FCSTD DOCUMENT  (FreeCAD 0.18R15671 (Git))
Label: IL_2_Verify
License: All rights reserved
LicenseURL: http://en.wikipedia.org/wiki/All_rights_reserved
objects: Part::Part2DObjectPython×100, App::DocumentObjectGroup×5, Sketcher::SketchObjectPython×1
note: 101 computed .brp shape members not serialized (recipe doc carries the construction recipe); baked Part::Feature solids carry a one-line shape summary decoded from their .brp

FEATURE [Part::Part2DObjectPython] Line  # Draft 2D object (typed FeaturePython)
  ChamferSize = 0
  Closed = false
  End = (406185,16682.9,0)
  FilletRadius = 0
  Length = 406527
  MakeFace = false
  Points = (2) [(0,0,0),(406185,16682.9,0)]
  Start = (0,0,0)
  Subdivisions = 0
FEATURE [Part::Part2DObjectPython] Line001  # Draft 2D object (typed FeaturePython)
  ChamferSize = 0
  Closed = false
  End = (393568,323876,0)
  FilletRadius = 0
  Length = 307452
  MakeFace = true
  Placement = pos=(406185,16682.9,0) rot=(0,0,1;0rad)
  Points = (2) [(0,0,0),(-12616.9,307193,0)]
  Start = (406185,16682.9,0)
  Subdivisions = 0
FEATURE [Part::Part2DObjectPython] Arc  # Draft 2D object (typed FeaturePython)
  FirstAngle = -87.6481
  LastAngle = -38.8387
  MakeFace = true
  Placement = pos=(393568,323876,0) rot=(0,0,1;0rad)
  Radius = 307452
FEATURE [Part::Part2DObjectPython] Line002  # Draft 2D object (typed FeaturePython)
  ChamferSize = 0
  Closed = false
  End = (158220,513361,0)
  FilletRadius = 0
  Length = 609600
  MakeFace = true
  Placement = pos=(633047,131064,0) rot=(0,0,1;0rad)
  Points = (2) [(0,0,0),(-474827,382298,0)]
  Start = (633047,131064,0)
  Subdivisions = 0
FEATURE [Part::Part2DObjectPython] Arc001  # Draft 2D object (typed FeaturePython)
  FirstAngle = -38.8386
  LastAngle = -29.9144
  MakeFace = true
  Placement = pos=(158220,513361,0) rot=(0,0,1;0rad)
  Radius = 609600
FEATURE [Part::Part2DObjectPython] Line003  # Draft 2D object (typed FeaturePython)
  ChamferSize = 0
  Closed = false
  End = (823746,447710,0)
  FilletRadius = 0
  Length = 274997
  MakeFace = true
  Placement = pos=(686603,209350,0) rot=(0,0,1;0rad)
  Points = (2) [(0,0,0),(137143,238359,0)]
  Start = (686603,209350,0)
  Subdivisions = 0
FEATURE [Part::Part2DObjectPython] Line009  # Draft 2D object (typed FeaturePython)
  ChamferSize = 0
  Closed = false
  End = (-180183,1.02533e+06,0)
  FilletRadius = 0
  Length = 1158240
  MakeFace = true
  Placement = pos=(823746,447710,0) rot=(0,0,1;0rad)
  Points = (2) [(0,0,0),(-1003930,577622,0)]
  Start = (823746,447710,0)
  Subdivisions = 0
FEATURE [Part::Part2DObjectPython] Arc005  # Draft 2D object (typed FeaturePython)
  FirstAngle = -29.9144
  LastAngle = 10.7592
  MakeFace = true
  Placement = pos=(-180183,1.02533e+06,0) rot=(0,0,1;0rad)
  Radius = 1158240
FEATURE [Part::Part2DObjectPython] Line010  # Draft 2D object (typed FeaturePython)
  ChamferSize = 0
  Closed = false
  End = (943133,1.31819e+06,0)
  FilletRadius = 0
  Length = 78008.6
  MakeFace = true
  Placement = pos=(957696,1.24155e+06,0) rot=(0,0,1;0rad)
  Points = (2) [(0,0,0),(-14562.8,76637.2,0)]
  Start = (957696,1.24155e+06,0)
  Subdivisions = 0
FEATURE [Part::Part2DObjectPython] Line011  # Draft 2D object (typed FeaturePython)
  ChamferSize = 0
  Closed = false
  End = (1.63185e+06,1.44906e+06,0)
  FilletRadius = 0
  Length = 701040
  MakeFace = true
  Placement = pos=(943133,1.31819e+06,0) rot=(0,0,1;0rad)
  Points = (2) [(0,0,0),(688716,130871,0)]
  Start = (943133,1.31819e+06,0)
  Subdivisions = 0
FEATURE [Part::Part2DObjectPython] Arc006  # Draft 2D object (typed FeaturePython)
  FirstAngle = -179.348
  LastAngle = -169.241
  MakeFace = true
  Placement = pos=(1.63185e+06,1.44906e+06,0) rot=(0,0,1;0rad)
  Radius = 701040
FEATURE [Part::Part2DObjectPython] Line012  # Draft 2D object (typed FeaturePython)
  ChamferSize = 0
  Closed = false
  End = (930155,1.50255e+06,0)
  FilletRadius = 0
  Length = 61471
  MakeFace = true
  Placement = pos=(930855,1.44108e+06,0) rot=(0,0,1;0rad)
  Points = (2) [(0,0,0),(-699.39,61467,0)]
  Start = (930855,1.44108e+06,0)
  Subdivisions = 0
FEATURE [Part::Part2DObjectPython] Line013  # Draft 2D object (typed FeaturePython)
  ChamferSize = 0
  Closed = false
  End = (2.14928e+06,1.51642e+06,0)
  FilletRadius = 0
  Length = 1.2192e+06
  MakeFace = true
  Placement = pos=(930155,1.50255e+06,0) rot=(0,0,1;0rad)
  Points = (2) [(0,0,0),(1219120,13871.5,0)]
  Start = (930155,1.50255e+06,0)
  Subdivisions = 0
FEATURE [Part::Part2DObjectPython] Arc007  # Draft 2D object (typed FeaturePython)
  FirstAngle = -186.169
  LastAngle = -179.348
  MakeFace = true
  Placement = pos=(2.14928e+06,1.51642e+06,0) rot=(0,0,1;0rad)
  Radius = 1.2192e+06
FEATURE [Part::Part2DObjectPython] Line014  # Draft 2D object (typed FeaturePython)
  ChamferSize = 0
  Closed = false
  End = (1.54321e+06,1.58193e+06,0)
  FilletRadius = 0
  Length = 609600
  MakeFace = true
  Placement = pos=(937137,1.64744e+06,0) rot=(0,0,1;0rad)
  Points = (2) [(0,0,0),(606070,-65510.3,0)]
  Start = (937137,1.64744e+06,0)
  Subdivisions = 0
FEATURE [Part::Part2DObjectPython] Arc008  # Draft 2D object (typed FeaturePython)
  FirstAngle = 155.568
  LastAngle = 173.831
  MakeFace = true
  Placement = pos=(1.54321e+06,1.58193e+06,0) rot=(0,0,1;0rad)
  Radius = 609600
FEATURE [Part::Part2DObjectPython] Line015  # Draft 2D object (typed FeaturePython)
  ChamferSize = 0
  Closed = false
  End = (1.02017e+06,1.90446e+06,0)
  FilletRadius = 0
  Length = 77313
  MakeFace = true
  Placement = pos=(988196,1.83407e+06,0) rot=(0,0,1;0rad)
  Points = (2) [(0,0,0),(31977.9,70389.7,0)]
  Start = (988196,1.83407e+06,0)
  Subdivisions = 0
FEATURE [Part::Part2DObjectPython] Line016  # Draft 2D object (typed FeaturePython)
  ChamferSize = 0
  Closed = false
  End = (580180,2.10435e+06,0)
  FilletRadius = 0
  Length = 483270
  MakeFace = true
  Placement = pos=(1.02017e+06,1.90446e+06,0) rot=(0,0,1;0rad)
  Points = (2) [(0,0,0),(-439994,199888,0)]
  Start = (1.02017e+06,1.90446e+06,0)
  Subdivisions = 0
FEATURE [Part::Part2DObjectPython] Arc009  # Draft 2D object (typed FeaturePython)
  FirstAngle = -24.4322
  LastAngle = 4.90889
  MakeFace = true
  Placement = pos=(580180,2.10435e+06,0) rot=(0,0,1;0rad)
  Radius = 483270
FEATURE [Part::Part2DObjectPython] Line017  # Draft 2D object (typed FeaturePython)
  ChamferSize = 0
  Closed = false
  End = (1.05283e+06,2.24875e+06,0)
  FilletRadius = 0
  Length = 103421
  MakeFace = true
  Placement = pos=(1.06168e+06,2.14571e+06,0) rot=(0,0,1;0rad)
  Points = (2) [(0,0,0),(-8849.91,103042,0)]
  Start = (1.06168e+06,2.14571e+06,0)
  Subdivisions = 0
FEATURE [Part::Part2DObjectPython] Line018  # Draft 2D object (typed FeaturePython)
  ChamferSize = 0
  Closed = false
  End = (2.14608e+06,2.34264e+06,0)
  FilletRadius = 0
  Length = 1097280
  MakeFace = true
  Placement = pos=(1.05283e+06,2.24875e+06,0) rot=(0,0,1;0rad)
  Points = (2) [(0,0,0),(1093260,93896.1,0)]
  Start = (1.05283e+06,2.24875e+06,0)
  Subdivisions = 0
FEATURE [Part::Part2DObjectPython] Arc010  # Draft 2D object (typed FeaturePython)
  FirstAngle = -192.975
  LastAngle = -175.091
  MakeFace = true
  Placement = pos=(2.14608e+06,2.34264e+06,0) rot=(0,0,1;0rad)
  Radius = 1.09728e+06
FEATURE [Part::Part2DObjectPython] Line019  # Draft 2D object (typed FeaturePython)
  ChamferSize = 0
  Closed = false
  End = (1.13352e+06,2.8351e+06,0)
  FilletRadius = 0
  Length = 252532
  MakeFace = true
  Placement = pos=(1.07682e+06,2.58901e+06,0) rot=(0,0,1;0rad)
  Points = (2) [(0,0,0),(56700,246084,0)]
  Start = (1.07682e+06,2.58901e+06,0)
  Subdivisions = 0
FEATURE [Part::Part2DObjectPython] Line020  # Draft 2D object (typed FeaturePython)
  ChamferSize = 0
  Closed = false
  End = (2.91563e+06,2.42448e+06,0)
  FilletRadius = 0
  Length = 1828800
  MakeFace = true
  Placement = pos=(1.13352e+06,2.8351e+06,0) rot=(0,0,1;0rad)
  Points = (2) [(0,0,0),(1782110,-410613,0)]
  Start = (1.13352e+06,2.8351e+06,0)
  Subdivisions = 0
FEATURE [Part::Part2DObjectPython] Arc011  # Draft 2D object (typed FeaturePython)
  FirstAngle = 153.126
  LastAngle = 167.025
  MakeFace = true
  Placement = pos=(2.91563e+06,2.42448e+06,0) rot=(0,0,1;0rad)
  Radius = 1.8288e+06
FEATURE [Part::Part2DObjectPython] Line021  # Draft 2D object (typed FeaturePython)
  ChamferSize = 0
  Closed = false
  End = (2.23592e+06,2.76894e+06,0)
  FilletRadius = 0
  Length = 1066800
  MakeFace = true
  Placement = pos=(1.28434e+06,3.25117e+06,0) rot=(0,0,1;0rad)
  Points = (2) [(0,0,0),(951585,-482232,0)]
  Start = (1.28434e+06,3.25117e+06,0)
  Subdivisions = 0
FEATURE [Part::Part2DObjectPython] Arc012  # Draft 2D object (typed FeaturePython)
  FirstAngle = 143.778
  LastAngle = 153.126
  MakeFace = true
  Placement = pos=(2.23592e+06,2.76894e+06,0) rot=(0,0,1;0rad)
  Radius = 1.0668e+06
FEATURE [Part::Part2DObjectPython] Line022  # Draft 2D object (typed FeaturePython)
  ChamferSize = 0
  Closed = false
  End = (1.91525e+06,4.13648e+06,0)
  FilletRadius = 0
  Length = 913758
  MakeFace = true
  Placement = pos=(1.3753e+06,3.39932e+06,0) rot=(0,0,1;0rad)
  Points = (2) [(0,0,0),(539954,737159,0)]
  Start = (1.3753e+06,3.39932e+06,0)
  Subdivisions = 0
FEATURE [Part::Part2DObjectPython] Line023  # Draft 2D object (typed FeaturePython)
  ChamferSize = 0
  Closed = false
  End = (2.89882e+06,3.41604e+06,0)
  FilletRadius = 0
  Length = 1.2192e+06
  MakeFace = true
  Placement = pos=(1.91525e+06,4.13648e+06,0) rot=(0,0,1;0rad)
  Points = (2) [(0,0,0),(983569,-720444,0)]
  Start = (1.91525e+06,4.13648e+06,0)
  Subdivisions = 0
FEATURE [Part::Part2DObjectPython] Arc013  # Draft 2D object (typed FeaturePython)
  FirstAngle = 138.795
  LastAngle = 143.778
  MakeFace = true
  Placement = pos=(2.89882e+06,3.41604e+06,0) rot=(0,0,1;0rad)
  Radius = 1219200
FEATURE [Part::Part2DObjectPython] Line024  # Draft 2D object (typed FeaturePython)
  ChamferSize = 0
  Closed = false
  End = (2.00002e+06,4.24029e+06,0)
  FilletRadius = 0
  Length = 28041.6
  MakeFace = true
  Placement = pos=(1.98154e+06,4.21919e+06,0) rot=(0,0,1;0rad)
  Points = (2) [(0,0,0),(18472.5,21097.3,0)]
  Start = (1.98154e+06,4.21919e+06,0)
  Subdivisions = 0
FEATURE [Part::Part2DObjectPython] Line025  # Draft 2D object (typed FeaturePython)
  ChamferSize = 0
  Closed = false
  End = (-293170,6.24817e+06,0)
  FilletRadius = 0
  Length = 3048000
  MakeFace = true
  Placement = pos=(2.00002e+06,4.24029e+06,0) rot=(0,0,1;0rad)
  Points = (2) [(0,0,0),(-2293190,2007890,0)]
  Start = (2.00002e+06,4.24029e+06,0)
  Subdivisions = 0
FEATURE [Part::Part2DObjectPython] Arc014  # Draft 2D object (typed FeaturePython)
  FirstAngle = -41.205
  LastAngle = -38.3406
  MakeFace = true
  Placement = pos=(-293170,6.24817e+06,0) rot=(0,0,1;0rad)
  Radius = 3.048e+06
FEATURE [Part::Part2DObjectPython] Line026  # Draft 2D object (typed FeaturePython)
  ChamferSize = 0
  Closed = false
  End = (2.21427e+06,4.50504e+06,0)
  FilletRadius = 0
  Length = 188244
  MakeFace = true
  Placement = pos=(2.09749e+06,4.35739e+06,0) rot=(0,0,1;0rad)
  Points = (2) [(0,0,0),(116774,147647,0)]
  Start = (2.09749e+06,4.35739e+06,0)
  Subdivisions = 0
FEATURE [Part::Part2DObjectPython] Line027  # Draft 2D object (typed FeaturePython)
  ChamferSize = 0
  Closed = false
  End = (2.6924e+06,4.12688e+06,0)
  FilletRadius = 0
  Length = 609600
  MakeFace = true
  Placement = pos=(2.21427e+06,4.50504e+06,0) rot=(0,0,1;0rad)
  Points = (2) [(0,0,0),(478132,-378156,0)]
  Start = (2.21427e+06,4.50504e+06,0)
  Subdivisions = 0
FEATURE [Part::Part2DObjectPython] Arc015  # Draft 2D object (typed FeaturePython)
  FirstAngle = 121.776
  LastAngle = 141.659
  MakeFace = true
  Placement = pos=(2.6924e+06,4.12688e+06,0) rot=(0,0,1;0rad)
  Radius = 609600
FEATURE [Part::Part2DObjectPython] Line028  # Draft 2D object (typed FeaturePython)
  ChamferSize = 0
  Closed = false
  End = (2.56738e+06,4.76653e+06,0)
  FilletRadius = 0
  Length = 230563
  MakeFace = true
  Placement = pos=(2.37138e+06,4.64511e+06,0) rot=(0,0,1;0rad)
  Points = (2) [(0,0,0),(196004,121416,0)]
  Start = (2.37138e+06,4.64511e+06,0)
  Subdivisions = 0
FEATURE [Part::Part2DObjectPython] Line029  # Draft 2D object (typed FeaturePython)
  ChamferSize = 0
  Closed = false
  End = (3.17963e+06,3.77816e+06,0)
  FilletRadius = 0
  Length = 1162630
  MakeFace = true
  Placement = pos=(2.56738e+06,4.76653e+06,0) rot=(0,0,1;0rad)
  Points = (2) [(0,0,0),(612248,-988363,0)]
  Start = (2.56738e+06,4.76653e+06,0)
  Subdivisions = 0
FEATURE [Part::Part2DObjectPython] Arc016  # Draft 2D object (typed FeaturePython)
  FirstAngle = 107.677
  LastAngle = 121.776
  MakeFace = true
  Placement = pos=(3.17963e+06,3.77816e+06,0) rot=(0,0,1;0rad)
  Radius = 1.16263e+06
FEATURE [Part::Part2DObjectPython] Line030  # Draft 2D object (typed FeaturePython)
  ChamferSize = 0
  Closed = false
  End = (3.03557e+06,4.23019e+06,0)
  FilletRadius = 0
  Length = 688199
  MakeFace = true
  Placement = pos=(2.82659e+06,4.8859e+06,0) rot=(0,0,1;0rad)
  Points = (2) [(0,0,0),(208974,-655704,0)]
  Start = (2.82659e+06,4.8859e+06,0)
  Subdivisions = 0
FEATURE [Part::Part2DObjectPython] Arc017  # Draft 2D object (typed FeaturePython)
  FirstAngle = 73.1156
  LastAngle = 107.677
  MakeFace = true
  Placement = pos=(3.03557e+06,4.23019e+06,0) rot=(0,0,1;0rad)
  Radius = 688199
FEATURE [Part::Part2DObjectPython] Line031  # Draft 2D object (typed FeaturePython)
  ChamferSize = 0
  Closed = false
  End = (3.29632e+06,4.87025e+06,0)
  FilletRadius = 0
  Length = 63614.8
  MakeFace = true
  Placement = pos=(3.23545e+06,4.88872e+06,0) rot=(0,0,1;0rad)
  Points = (2) [(0,0,0),(60872.5,-18476.4,0)]
  Start = (3.23545e+06,4.88872e+06,0)
  Subdivisions = 0
FEATURE [Part::Part2DObjectPython] Line032  # Draft 2D object (typed FeaturePython)
  ChamferSize = 0
  Closed = false
  End = (3.54552e+06,5.69127e+06,0)
  FilletRadius = 0
  Length = 858012
  MakeFace = true
  Placement = pos=(3.29632e+06,4.87025e+06,0) rot=(0,0,1;0rad)
  Points = (2) [(0,0,0),(249202,821025,0)]
  Start = (3.29632e+06,4.87025e+06,0)
  Subdivisions = 0
FEATURE [Part::Part2DObjectPython] Arc018  # Draft 2D object (typed FeaturePython)
  FirstAngle = -106.884
  LastAngle = -69.0486
  MakeFace = true
  Placement = pos=(3.54552e+06,5.69127e+06,0) rot=(0,0,1;0rad)
  Radius = 858012
FEATURE [Part::Part2DObjectPython] Line033  # Draft 2D object (typed FeaturePython)
  ChamferSize = 0
  Closed = false
  End = (4.42061e+06,5.10758e+06,0)
  FilletRadius = 0
  Length = 608515
  MakeFace = true
  Placement = pos=(3.85233e+06,4.88999e+06,0) rot=(0,0,1;0rad)
  Points = (2) [(0,0,0),(568282,217590,0)]
  Start = (3.85233e+06,4.88999e+06,0)
  Subdivisions = 0
FEATURE [Part::Part2DObjectPython] Line034  # Draft 2D object (typed FeaturePython)
  ChamferSize = 0
  Closed = false
  End = (4.25495e+06,5.54024e+06,0)
  FilletRadius = 0
  Length = 463296
  MakeFace = true
  Placement = pos=(4.42061e+06,5.10758e+06,0) rot=(0,0,1;0rad)
  Points = (2) [(0,0,0),(-165663,432665,0)]
  Start = (4.42061e+06,5.10758e+06,0)
  Subdivisions = 0
FEATURE [Part::Part2DObjectPython] Arc019  # Draft 2D object (typed FeaturePython)
  FirstAngle = -69.0486
  LastAngle = -32.2072
  MakeFace = true
  Placement = pos=(4.25495e+06,5.54024e+06,0) rot=(0,0,1;0rad)
  Radius = 463296
FEATURE [Part::Part2DObjectPython] Line035  # Draft 2D object (typed FeaturePython)
  ChamferSize = 0
  Closed = false
  End = (4.67944e+06,5.3449e+06,0)
  FilletRadius = 0
  Length = 60960
  MakeFace = true
  Placement = pos=(4.64695e+06,5.29332e+06,0) rot=(0,0,1;0rad)
  Points = (2) [(0,0,0),(32490.6,51579.8,0)]
  Start = (4.64695e+06,5.29332e+06,0)
  Subdivisions = 0
FEATURE [Part::Part2DObjectPython] Line036  # Draft 2D object (typed FeaturePython)
  ChamferSize = 0
  Closed = false
  End = (5.22103e+06,5.00374e+06,0)
  FilletRadius = 0
  Length = 640080
  MakeFace = true
  Placement = pos=(4.67944e+06,5.3449e+06,0) rot=(0,0,1;0rad)
  Points = (2) [(0,0,0),(541588,-341152,0)]
  Start = (4.67944e+06,5.3449e+06,0)
  Subdivisions = 0
FEATURE [Part::Part2DObjectPython] Arc020  # Draft 2D object (typed FeaturePython)
  FirstAngle = 136.32
  LastAngle = 147.793
  MakeFace = true
  Placement = pos=(5.22103e+06,5.00374e+06,0) rot=(0,0,1;0rad)
  Radius = 640080
FEATURE [Part::Part2DObjectPython] Line037  # Draft 2D object (typed FeaturePython)
  ChamferSize = 0
  Closed = false
  End = (5.11486e+06,5.81937e+06,0)
  FilletRadius = 0
  Length = 516539
  MakeFace = true
  Placement = pos=(4.75812e+06,5.4458e+06,0) rot=(0,0,1;0rad)
  Points = (2) [(0,0,0),(356737,373565,0)]
  Start = (4.75812e+06,5.4458e+06,0)
  Subdivisions = 0
FEATURE [Part::Part2DObjectPython] Line038  # Draft 2D object (typed FeaturePython)
  ChamferSize = 0
  Closed = false
  End = (5.66594e+06,5.29311e+06,0)
  FilletRadius = 0
  Length = 762000
  MakeFace = true
  Placement = pos=(5.11486e+06,5.81937e+06,0) rot=(0,0,1;0rad)
  Points = (2) [(0,0,0),(551085,-526260,0)]
  Start = (5.11486e+06,5.81937e+06,0)
  Subdivisions = 0
FEATURE [Part::Part2DObjectPython] Arc025  # Draft 2D object (typed FeaturePython)
  FirstAngle = 96.3367
  LastAngle = 136.32
  MakeFace = true
  Placement = pos=(5.66594e+06,5.29311e+06,0) rot=(0,0,1;0rad)
  Radius = 762000
FEATURE [Part::Part2DObjectPython] Line039  # Draft 2D object (typed FeaturePython)
  ChamferSize = 0
  Closed = false
  End = (5.65333e+06,6.05839e+06,0)
  FilletRadius = 0
  Length = 71932.8
  MakeFace = true
  Placement = pos=(5.58184e+06,6.05045e+06,0) rot=(0,0,1;0rad)
  Points = (2) [(0,0,0),(71493.3,7939.29,0)]
  Start = (5.58184e+06,6.05045e+06,0)
  Subdivisions = 0
FEATURE [Part::Part2DObjectPython] Line040  # Draft 2D object (typed FeaturePython)
  ChamferSize = 0
  Closed = false
  End = (5.5398e+06,7.08081e+06,0)
  FilletRadius = 0
  Length = 1.0287e+06
  MakeFace = true
  Placement = pos=(5.65333e+06,6.05839e+06,0) rot=(0,0,1;0rad)
  Points = (2) [(0,0,0),(-113539,1022420,0)]
  Start = (5.65333e+06,6.05839e+06,0)
  Subdivisions = 0
FEATURE [Part::Part2DObjectPython] Arc026  # Draft 2D object (typed FeaturePython)
  FirstAngle = -83.6633
  LastAngle = -64.1411
  MakeFace = true
  Placement = pos=(5.5398e+06,7.08081e+06,0) rot=(0,0,1;0rad)
  Radius = 1.0287e+06
FEATURE [Part::Part2DObjectPython] Line041  # Draft 2D object (typed FeaturePython)
  ChamferSize = 0
  Closed = false
  End = (6.36716e+06,6.33866e+06,0)
  FilletRadius = 0
  Length = 420832
  MakeFace = true
  Placement = pos=(5.98847e+06,6.15511e+06,0) rot=(0,0,1;0rad)
  Points = (2) [(0,0,0),(378694,183549,0)]
  Start = (5.98847e+06,6.15511e+06,0)
  Subdivisions = 0
FEATURE [Part::Part2DObjectPython] Line042  # Draft 2D object (typed FeaturePython)
  ChamferSize = 0
  Closed = false
  End = (6.67211e+06,5.7095e+06,0)
  FilletRadius = 0
  Length = 699162
  MakeFace = true
  Placement = pos=(6.36716e+06,6.33866e+06,0) rot=(0,0,1;0rad)
  Points = (2) [(0,0,0),(304944,-629156,0)]
  Start = (6.36716e+06,6.33866e+06,0)
  Subdivisions = 0
FEATURE [Part::Part2DObjectPython] Arc027  # Draft 2D object (typed FeaturePython)
  FirstAngle = 99.3106
  LastAngle = 115.859
  MakeFace = true
  Placement = pos=(6.67211e+06,5.7095e+06,0) rot=(0,0,1;0rad)
  Radius = 699162
FEATURE [Part::Part2DObjectPython] Line043  # Draft 2D object (typed FeaturePython)
  ChamferSize = 0
  Closed = false
  End = (7.54438e+06,6.561e+06,0)
  FilletRadius = 0
  Length = 998544
  MakeFace = true
  Placement = pos=(6.55899e+06,6.39945e+06,0) rot=(0,0,1;0rad)
  Points = (2) [(0,0,0),(985389,161551,0)]
  Start = (6.55899e+06,6.39945e+06,0)
  Subdivisions = 0
FEATURE [Part::Part2DObjectPython] Line044  # Draft 2D object (typed FeaturePython)
  ChamferSize = 0
  Closed = false
  End = (7.84026e+06,4.7563e+06,0)
  FilletRadius = 0
  Length = 1.8288e+06
  MakeFace = true
  Placement = pos=(7.54438e+06,6.561e+06,0) rot=(0,0,1;0rad)
  Points = (2) [(0,0,0),(295875,-1804710,0)]
  Start = (7.54438e+06,6.561e+06,0)
  Subdivisions = 0
FEATURE [Part::Part2DObjectPython] Arc028  # Draft 2D object (typed FeaturePython)
  FirstAngle = 91.8839
  LastAngle = 99.3106
  MakeFace = true
  Placement = pos=(7.84026e+06,4.7563e+06,0) rot=(0,0,1;0rad)
  Radius = 1828800
FEATURE [Part::Part2DObjectPython] Line045  # Draft 2D object (typed FeaturePython)
  ChamferSize = 0
  Closed = false
  End = (7.84907e+06,6.58638e+06,0)
  FilletRadius = 0
  Length = 68969.2
  MakeFace = true
  Placement = pos=(7.78014e+06,6.58411e+06,0) rot=(0,0,1;0rad)
  Points = (2) [(0,0,0),(68931.9,2267.32,0)]
  Start = (7.78014e+06,6.58411e+06,0)
  Subdivisions = 0
FEATURE [Part::Part2DObjectPython] Line046  # Draft 2D object (typed FeaturePython)
  ChamferSize = 0
  Closed = false
  End = (7.83103e+06,7.13472e+06,0)
  FilletRadius = 0
  Length = 548640
  MakeFace = true
  Placement = pos=(7.84907e+06,6.58638e+06,0) rot=(0,0,1;0rad)
  Points = (2) [(0,0,0),(-18036.2,548343,0)]
  Start = (7.84907e+06,6.58638e+06,0)
  Subdivisions = 0
FEATURE [Part::Part2DObjectPython] Arc029  # Draft 2D object (typed FeaturePython)
  FirstAngle = -88.1161
  LastAngle = -77.9325
  MakeFace = true
  Placement = pos=(7.83103e+06,7.13472e+06,0) rot=(0,0,1;0rad)
  Radius = 548640
FEATURE [Part::Part2DObjectPython] Line047  # Draft 2D object (typed FeaturePython)
  ChamferSize = 0
  Closed = false
  End = (8.03927e+06,6.6182e+06,0)
  FilletRadius = 0
  Length = 95650.2
  MakeFace = true
  Placement = pos=(7.94573e+06,6.5982e+06,0) rot=(0,0,1;0rad)
  Points = (2) [(0,0,0),(93536.5,19997,0)]
  Start = (7.94573e+06,6.5982e+06,0)
  Subdivisions = 0
FEATURE [Part::Part2DObjectPython] Line048  # Draft 2D object (typed FeaturePython)
  ChamferSize = 0
  Closed = false
  End = (7.92457e+06,7.15472e+06,0)
  FilletRadius = 0
  Length = 548640
  MakeFace = true
  Placement = pos=(8.03927e+06,6.6182e+06,0) rot=(0,0,1;0rad)
  Points = (2) [(0,0,0),(-114701,536516,0)]
  Start = (8.03927e+06,6.6182e+06,0)
  Subdivisions = 0
FEATURE [Part::Part2DObjectPython] Arc030  # Draft 2D object (typed FeaturePython)
  FirstAngle = -77.9325
  LastAngle = -62.4842
  MakeFace = true
  Placement = pos=(7.92457e+06,7.15472e+06,0) rot=(0,0,1;0rad)
  Radius = 548640
FEATURE [Part::Part2DObjectPython] Line049  # Draft 2D object (typed FeaturePython)
  ChamferSize = 0
  Closed = false
  End = (1.09943e+07,1.26169e+06,0)
  FilletRadius = 0
  Length = 6.096e+06
  MakeFace = true
  Placement = pos=(8.17804e+06,6.66814e+06,0) rot=(0,0,1;0rad)
  Points = (2) [(0,0,0),(2816310,-5406440,0)]
  Start = (8.17804e+06,6.66814e+06,0)
  Subdivisions = 0
FEATURE [Part::Part2DObjectPython] Arc031  # Draft 2D object (typed FeaturePython)
  FirstAngle = 116.064
  LastAngle = 117.516
  MakeFace = true
  Placement = pos=(1.09943e+07,1.26169e+06,0) rot=(0,0,1;0rad)
  Radius = 6.096e+06
FEATURE [Part::Part2DObjectPython] Line050  # Draft 2D object (typed FeaturePython)
  ChamferSize = 0
  Closed = false
  End = (8.53989e+06,6.8473e+06,0)
  FilletRadius = 0
  Length = 249320
  MakeFace = true
  Placement = pos=(8.31593e+06,6.73776e+06,0) rot=(0,0,1;0rad)
  Points = (2) [(0,0,0),(223965,109545,0)]
  Start = (8.31593e+06,6.73776e+06,0)
  Subdivisions = 0
FEATURE [Part::Part2DObjectPython] Line051  # Draft 2D object (typed FeaturePython)
  ChamferSize = 0
  Closed = false
  End = (8.15369e+06,7.63689e+06,0)
  FilletRadius = 0
  Length = 878976
  MakeFace = true
  Placement = pos=(8.53989e+06,6.8473e+06,0) rot=(0,0,1;0rad)
  Points = (2) [(0,0,0),(-386199,789588,0)]
  Start = (8.53989e+06,6.8473e+06,0)
  Subdivisions = 0
FEATURE [Part::Part2DObjectPython] Arc032  # Draft 2D object (typed FeaturePython)
  FirstAngle = -63.9361
  LastAngle = -50.4225
  MakeFace = true
  Placement = pos=(8.15369e+06,7.63689e+06,0) rot=(0,0,1;0rad)
  Radius = 878976
FEATURE [Part::Part2DObjectPython] Line052  # Draft 2D object (typed FeaturePython)
  ChamferSize = 0
  Closed = false
  End = (8.80895e+06,7.03814e+06,0)
  FilletRadius = 0
  Length = 123569
  MakeFace = true
  Placement = pos=(8.71371e+06,6.95941e+06,0) rot=(0,0,1;0rad)
  Points = (2) [(0,0,0),(95242.5,78728.4,0)]
  Start = (8.71371e+06,6.95941e+06,0)
  Subdivisions = 0
FEATURE [Part::Part2DObjectPython] Line053  # Draft 2D object (typed FeaturePython)
  ChamferSize = 0
  Closed = false
  End = (9.46436e+06,6.24525e+06,0)
  FilletRadius = 0
  Length = 1028700
  MakeFace = true
  Placement = pos=(8.80895e+06,7.03814e+06,0) rot=(0,0,1;0rad)
  Points = (2) [(0,0,0),(655407,-792884,0)]
  Start = (8.80895e+06,7.03814e+06,0)
  Subdivisions = 0
FEATURE [Part::Part2DObjectPython] Arc033  # Draft 2D object (typed FeaturePython)
  FirstAngle = 95.1656
  LastAngle = 129.578
  MakeFace = true
  Placement = pos=(9.46436e+06,6.24525e+06,0) rot=(0,0,1;0rad)
  Radius = 1.0287e+06
FEATURE [Part::Part2DObjectPython] Line054  # Draft 2D object (typed FeaturePython)
  ChamferSize = 0
  Closed = false
  End = (9.80575e+06,7.30901e+06,0)
  FilletRadius = 0
  Length = 435781
  MakeFace = true
  Placement = pos=(9.37174e+06,7.26978e+06,0) rot=(0,0,1;0rad)
  Points = (2) [(0,0,0),(434011,39235.4,0)]
  Start = (9.37174e+06,7.26978e+06,0)
  Subdivisions = 0
FEATURE [Part::Part2DObjectPython] Line055  # Draft 2D object (typed FeaturePython)
  ChamferSize = 0
  Closed = false
  End = (9.70455e+06,8.42849e+06,0)
  FilletRadius = 0
  Length = 1124040
  MakeFace = true
  Placement = pos=(9.80575e+06,7.30901e+06,0) rot=(0,0,1;0rad)
  Points = (2) [(0,0,0),(-101203,1119470,0)]
  Start = (9.80575e+06,7.30901e+06,0)
  Subdivisions = 0
FEATURE [Part::Part2DObjectPython] Arc034  # Draft 2D object (typed FeaturePython)
  FirstAngle = -84.8344
  LastAngle = -66.9158
  MakeFace = true
  Placement = pos=(9.70455e+06,8.42849e+06,0) rot=(0,0,1;0rad)
  Radius = 1.12404e+06
FEATURE [Part::Part2DObjectPython] Line056  # Draft 2D object (typed FeaturePython)
  ChamferSize = 0
  Closed = false
  End = (1.03509e+07,7.4821e+06,0)
  FilletRadius = 0
  Length = 223554
  MakeFace = true
  Placement = pos=(1.01453e+07,7.39445e+06,0) rot=(0,0,1;0rad)
  Points = (2) [(0,0,0),(205654,87651.8,0)]
  Start = (1.01453e+07,7.39445e+06,0)
  Subdivisions = 0
FEATURE [Part::Part2DObjectPython] Line057  # Draft 2D object (typed FeaturePython)
  ChamferSize = 0
  Closed = false
  End = (9.9446e+06,8.43544e+06,0)
  FilletRadius = 0
  Length = 1036320
  MakeFace = true
  Placement = pos=(1.03509e+07,7.4821e+06,0) rot=(0,0,1;0rad)
  Points = (2) [(0,0,0),(-406324,953341,0)]
  Start = (1.03509e+07,7.4821e+06,0)
  Subdivisions = 0
FEATURE [Part::Part2DObjectPython] Arc035  # Draft 2D object (typed FeaturePython)
  FirstAngle = -66.9158
  LastAngle = -33.6886
  MakeFace = true
  Placement = pos=(9.9446e+06,8.43544e+06,0) rot=(0,0,1;0rad)
  Radius = 1.03632e+06
FEATURE [Part::Part2DObjectPython] Line058  # Draft 2D object (typed FeaturePython)
  ChamferSize = 0
  Closed = false
  End = (1.09102e+07,8.01555e+06,0)
  FilletRadius = 0
  Length = 186199
  MakeFace = true
  Placement = pos=(1.08069e+07,7.86062e+06,0) rot=(0,0,1;0rad)
  Points = (2) [(0,0,0),(103281,154929,0)]
  Start = (1.08069e+07,7.86062e+06,0)
  Subdivisions = 0
FEATURE [Part::Part2DObjectPython] Line059  # Draft 2D object (typed FeaturePython)
  ChamferSize = 0
  Closed = false
  End = (1.20914e+07,7.22871e+06,0)
  FilletRadius = 0
  Length = 1.41928e+06
  MakeFace = true
  Placement = pos=(1.09102e+07,8.01555e+06,0) rot=(0,0,1;0rad)
  Points = (2) [(0,0,0),(1181210,-786832,0)]
  Start = (1.09102e+07,8.01555e+06,0)
  Subdivisions = 0
FEATURE [Part::Part2DObjectPython] Arc036  # Draft 2D object (typed FeaturePython)
  FirstAngle = 141.749
  LastAngle = 146.331
  MakeFace = true
  Placement = pos=(1.20914e+07,7.22871e+06,0) rot=(0,0,1;0rad)
  Radius = 1.41928e+06
FEATURE [Part::Part2DObjectPython] Line060  # Draft 2D object (typed FeaturePython)
  ChamferSize = 0
  Closed = false
  End = (1.10308e+07,8.17581e+06,0)
  FilletRadius = 0
  Length = 87131.2
  MakeFace = true
  Placement = pos=(1.09768e+07,8.10741e+06,0) rot=(0,0,1;0rad)
  Points = (2) [(0,0,0),(53968,68405.5,0)]
  Start = (1.09768e+07,8.10741e+06,0)
  Subdivisions = 0
FEATURE [Part::Part2DObjectPython] Line061  # Draft 2D object (typed FeaturePython)
  ChamferSize = 0
  Closed = false
  End = (1.03474e+07,8.71498e+06,0)
  FilletRadius = 0
  Length = 870487
  MakeFace = true
  Placement = pos=(1.10308e+07,8.17581e+06,0) rot=(0,0,1;0rad)
  Points = (2) [(0,0,0),(-683407,539169,0)]
  Start = (1.10308e+07,8.17581e+06,0)
  Subdivisions = 0
FEATURE [Part::Part2DObjectPython] Arc037  # Draft 2D object (typed FeaturePython)
  FirstAngle = -38.2714
  LastAngle = -26.6014
  MakeFace = true
  Placement = pos=(1.03474e+07,8.71498e+06,0) rot=(0,0,1;0rad)
  Radius = 870487
FEATURE [Part::Part2DObjectPython] Line062  # Draft 2D object (typed FeaturePython)
  ChamferSize = 0
  Closed = false
  End = (1.11686e+07,8.41077e+06,0)
  FilletRadius = 0
  Length = 95707.2
  MakeFace = true
  Placement = pos=(1.11257e+07,8.32519e+06,0) rot=(0,0,1;0rad)
  Points = (2) [(0,0,0),(42855.9,85576,0)]
  Start = (1.11257e+07,8.32519e+06,0)
  Subdivisions = 0
FEATURE [Part::Part2DObjectPython] Line063  # Draft 2D object (typed FeaturePython)
  ChamferSize = 0
  Closed = false
  End = (1.22587e+07,7.86484e+06,0)
  FilletRadius = 0
  Length = 1.2192e+06
  MakeFace = true
  Placement = pos=(1.11686e+07,8.41077e+06,0) rot=(0,0,1;0rad)
  Points = (2) [(0,0,0),(1090140,-545935,0)]
  Start = (1.11686e+07,8.41077e+06,0)
  Subdivisions = 0
FEATURE [Part::Part2DObjectPython] Arc038  # Draft 2D object (typed FeaturePython)
  FirstAngle = 134.678
  LastAngle = 153.399
  MakeFace = true
  Placement = pos=(1.22587e+07,7.86484e+06,0) rot=(0,0,1;0rad)
  Radius = 1.2192e+06
FEATURE [Part::Part2DObjectPython] Line064  # Draft 2D object (typed FeaturePython)
  ChamferSize = 0
  Closed = false
  End = (1.29445e+07,7.17129e+06,0)
  FilletRadius = 0
  Length = 2194560
  MakeFace = true
  Placement = pos=(1.14015e+07,8.73177e+06,0) rot=(0,0,1;0rad)
  Points = (2) [(0,0,0),(1543050,-1560480,0)]
  Start = (1.14015e+07,8.73177e+06,0)
  Subdivisions = 0
FEATURE [Part::Part2DObjectPython] Arc039  # Draft 2D object (typed FeaturePython)
  FirstAngle = 126.119
  LastAngle = 134.678
  MakeFace = true
  Placement = pos=(1.29445e+07,7.17129e+06,0) rot=(0,0,1;0rad)
  Radius = 2194560
FEATURE [Part::Part2DObjectPython] Line065  # Draft 2D object (typed FeaturePython)
  ChamferSize = 0
  Closed = false
  End = (1.1715e+07,8.99083e+06,0)
  FilletRadius = 0
  Length = 79388.5
  MakeFace = true
  Placement = pos=(1.16509e+07,8.94403e+06,0) rot=(0,0,1;0rad)
  Points = (2) [(0,0,0),(64129.3,46797.1,0)]
  Start = (1.16509e+07,8.94403e+06,0)
  Subdivisions = 0
FEATURE [Part::Part2DObjectPython] Line066  # Draft 2D object (typed FeaturePython)
  ChamferSize = 0
  Closed = false
  End = (1.09695e+07,1.00125e+07,0)
  FilletRadius = 0
  Length = 1.26477e+06
  MakeFace = true
  Placement = pos=(1.1715e+07,8.99083e+06,0) rot=(0,0,1;0rad)
  Points = (2) [(0,0,0),(-745544,1021670,0)]
  Start = (1.1715e+07,8.99083e+06,0)
  Subdivisions = 0
FEATURE [Part::Part2DObjectPython] Arc040  # Draft 2D object (typed FeaturePython)
  FirstAngle = -53.8806
  LastAngle = -42.3742
  MakeFace = true
  Placement = pos=(1.09695e+07,1.00125e+07,0) rot=(0,0,1;0rad)
  Radius = 1264770
FEATURE [Part::Part2DObjectPython] Line067  # Draft 2D object (typed FeaturePython)
  ChamferSize = 0
  Closed = false
  End = (1.19642e+07,9.2263e+06,0)
  FilletRadius = 0
  Length = 89635.3
  MakeFace = true
  Placement = pos=(1.19038e+07,9.16008e+06,0) rot=(0,0,1;0rad)
  Points = (2) [(0,0,0),(60411.5,66218.9,0)]
  Start = (1.19038e+07,9.16008e+06,0)
  Subdivisions = 0
FEATURE [Part::Part2DObjectPython] Line068  # Draft 2D object (typed FeaturePython)
  ChamferSize = 0
  Closed = false
  End = (1.21781e+07,9.03115e+06,0)
  FilletRadius = 0
  Length = 289560
  MakeFace = true
  Placement = pos=(1.19642e+07,9.2263e+06,0) rot=(0,0,1;0rad)
  Points = (2) [(0,0,0),(213915,-195155,0)]
  Start = (1.19642e+07,9.2263e+06,0)
  Subdivisions = 0
FEATURE [Part::Part2DObjectPython] Arc041  # Draft 2D object (typed FeaturePython)
  FirstAngle = 113.356
  LastAngle = 137.626
  MakeFace = true
  Placement = pos=(1.21781e+07,9.03115e+06,0) rot=(0,0,1;0rad)
  Radius = 289560
FEATURE [Part::Part2DObjectPython] Line069  # Draft 2D object (typed FeaturePython)
  ChamferSize = 0
  Closed = false
  End = (1.21252e+07,9.32368e+06,0)
  FilletRadius = 0
  Length = 67360.8
  MakeFace = true
  Placement = pos=(1.20633e+07,9.29698e+06,0) rot=(0,0,1;0rad)
  Points = (2) [(0,0,0),(61841,26705.1,0)]
  Start = (1.20633e+07,9.29698e+06,0)
  Subdivisions = 0
FEATURE [App::DocumentObjectGroup] Element_Lofts
FEATURE [Sketcher::SketchObjectPython] Default_Pavement  # WARN: FeaturePython — macro-defined, semantics opaque (R4)
  expr: Constraints[9] = Constraints.width * 0.014999999999999999
FEATURE [App::DocumentObjectGroup] Templates
  Group = -> [Default_Pavement]
FEATURE [App::DocumentObjectGroup] Group001  label="radii"
  Group = -> [Line068,Line066,Line064,Line063,Line061,Line059,Line057,Line055,Line053,Line051,Line049,Line048,Line046,Line044,Line042,Line040,Line038,Line036,Line034,Line032,Line030,Line029,Line027,Line025,Line023,Line021,Line020,Line018,Line016,Line014,Line013,Line011,Line009,Line002,Line001]
FEATURE [App::DocumentObjectGroup] Group002  label="geometry"
  Group = -> [Arc,Arc001,Arc005,Arc006,Arc007,Arc008,Arc009,Arc010,Arc011,Arc012,Arc013,Arc014,Arc015,Arc016,Arc017,Arc018,Arc019,Arc020,Arc025,Arc026,Arc027,Arc028,Arc029,Arc030,Arc031,Arc032,Arc033,Arc034,Arc035,Arc036,Arc037,Arc038,Arc039,Arc040,Arc041,Line067,Line069,Line065,Line062,Line060,Line058,Line056,Line054,Line052,Line050,Line047,Line045,Line041,Line039,Line037,Line035,Line033,Line031,Line028,+11 more]
FEATURE [App::DocumentObjectGroup] Group  label="SimpleGeometry"
  Group = -> [Group001,Group002]
